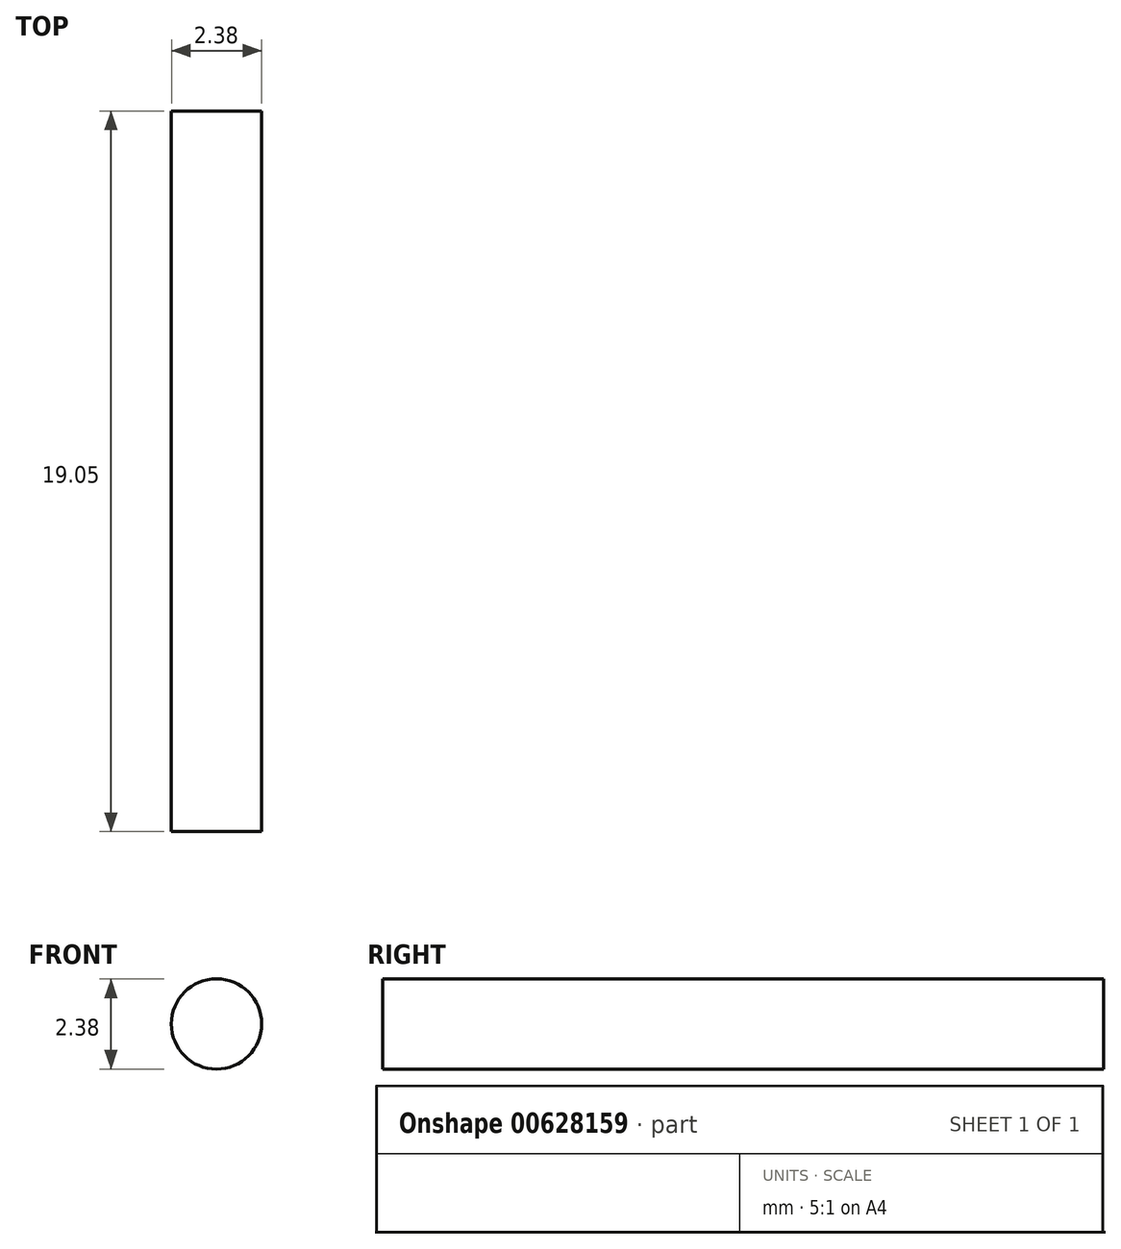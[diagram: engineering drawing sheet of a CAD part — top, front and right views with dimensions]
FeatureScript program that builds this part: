
annotation { "Feature Type Name" : "Feature", "Feature Type Description" : "" }
export const myFeature = defineFeature(function(context is Context, id is Id, definition is map)
    precondition{}
    {
        {
            var Q0;
            Q0=qCreatedBy(makeId("Front.planeOp"),FACE);
            var sketch = newSketch(context, id + "F0", { "sketchPlane" : qUnion([Q0])});
            skCircle(sketch, "E0", {"center": v(0, 0) * mm, "radius": 1.2 * mm});
            skSolve(sketch);
        }
        {
            var Q0;
            Q0=makeQuery(id+"F0.imprint","IMPRINT",FACE,{"disambiguationData":[TD([[makeQuery(id+"F0.imprint","IMPRINT",EDGE,{"derivedFrom":sQuery(id+"F0.wireOp",EDGE,"E0")}),1.0]])]});
            var Q1;
            Q1 = qConstructionFilter(qBodyType(qCreatedBy(id + "F0" ,EDGE), BodyType.WIRE), ConstructionObject.NO);
            extrude(context, id + "F1", {"entities" : qUnion([Q0]), "surfaceEntities" : qUnion([Q1]), "depth" : 19.05 * mm, "offsetDistance" : 25.4 * mm});
        }
    });
